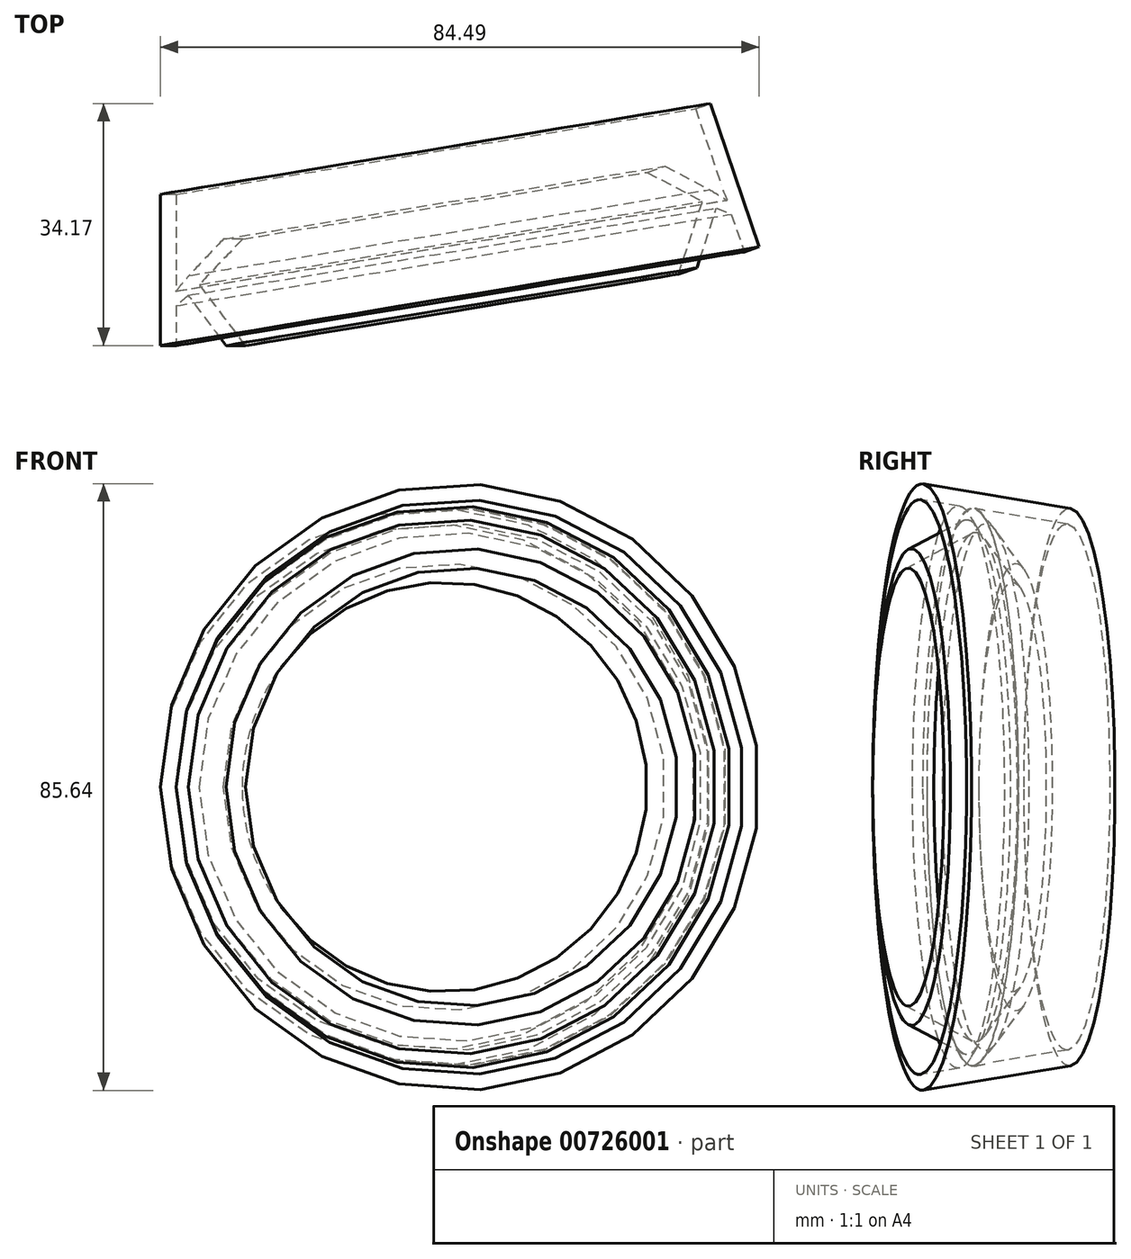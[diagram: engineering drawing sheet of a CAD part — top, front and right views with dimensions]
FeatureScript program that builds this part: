
annotation { "Feature Type Name" : "Feature", "Feature Type Description" : "" }
export const myFeature = defineFeature(function(context is Context, id is Id, definition is map)
    precondition{}
    {
        {
            var Q0;
            Q0=qCreatedBy(makeId("Top.planeOp"),FACE);
            var sketch = newSketch(context, id + "F0", { "sketchPlane" : qUnion([Q0])});
            skText(sketch, "E0", { "text": "akg", "fontName": "OpenSans-Regular.ttf"});
            const initialGuessF0  = {"E0": [-0.04364, 0.02039, 1, 0, 0.02023]};
            skSetInitialGuess(sketch, initialGuessF0);
            skSolve(sketch);
        }
        {
            var Q0;
            Q0 = qSketchRegion(id + "F0", true);
            var sketch = newSketch(context, id + "F1", { "sketchPlane" : qUnion([Q0])});
            skLineSegment(sketch, "E1", {"start": v(13.54, 46.12) * mm, "end": v(18.51, 16.05) * mm});
            skLineSegment(sketch, "E2", {"start": v(18.51, 16.05) * mm, "end": v(17.38, 22.88) * mm});
            skSolve(sketch);
        }
        {
            var Q0;
            Q0=makeQuery(id+"F1.imprint","IMPRINT",FACE,{"disambiguationData":[TD([[makeQuery(id+"F1.imprint","IMPRINT",EDGE,{"derivedFrom":makeQuery(id+"F0.imprint","IMPRINT",EDGE,{"derivedFrom":sQuery(id+"F0.wireOp",EDGE,"E0.sketch_text.stroke-19")})}),1.0]])]});
            var Q1;
            Q1=makeQuery(id+"F1.imprint","IMPRINT",FACE,{"disambiguationData":[TD([[makeQuery(id+"F1.imprint","IMPRINT",EDGE,{"derivedFrom":makeQuery(id+"F0.imprint","IMPRINT",EDGE,{"derivedFrom":sQuery(id+"F0.wireOp",EDGE,"E0.sketch_text.stroke-27")})}),-1.0]])]});
            var Q2;
            Q2=makeQuery(id+"F1.imprint","IMPRINT",FACE,{"disambiguationData":[TD([[makeQuery(id+"F1.imprint","IMPRINT",EDGE,{"derivedFrom":makeQuery(id+"F0.imprint","IMPRINT",EDGE,{"derivedFrom":sQuery(id+"F0.wireOp",EDGE,"E0.sketch_text.stroke-0")})}),-1.0]])]});
            var Q3;
            Q3=makeQuery(id+"F1.imprint","IMPRINT",FACE,{"disambiguationData":[TD([[makeQuery(id+"F1.imprint","IMPRINT",EDGE,{"derivedFrom":makeQuery(id+"F0.imprint","IMPRINT",EDGE,{"derivedFrom":sQuery(id+"F0.wireOp",EDGE,"E0.sketch_text.stroke-42")})}),-1.0]])]});
            var Q4;
            Q4=sQuery(id+"F1.wireOp",EDGE,"E1");
            revolve(context, id + "F2", {"surfaceOperationType" : NewSurfaceOperationType.NEW, "entities" : qUnion([Q0, Q1, Q2, Q3]), "axis" : qUnion([Q4]), "revolveType" : RevolveType.FULL});
        }
    });
